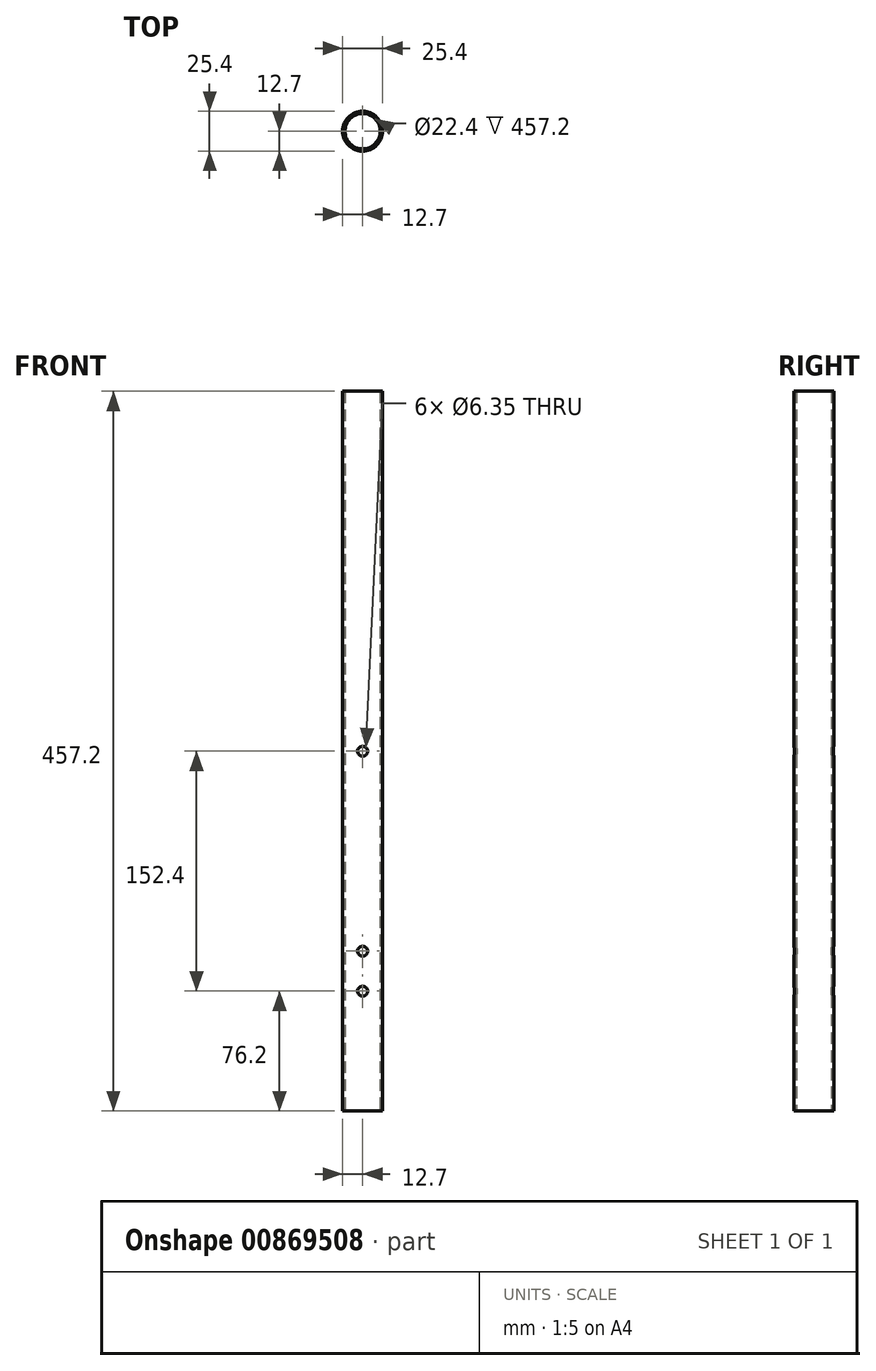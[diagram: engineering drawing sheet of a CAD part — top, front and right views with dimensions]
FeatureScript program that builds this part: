
annotation { "Feature Type Name" : "Feature", "Feature Type Description" : "" }
export const myFeature = defineFeature(function(context is Context, id is Id, definition is map)
    precondition{}
    {
        {
            var Q0;
            Q0=qCreatedBy(makeId("Top.planeOp"),FACE);
            var sketch = newSketch(context, id + "F0", { "sketchPlane" : qUnion([Q0])});
            skCircle(sketch, "E0", {"center": v(0, 0) * mm, "radius": 12.7 * mm});
            skCircle(sketch, "E1.0", {"center": v(0, 0) * mm, "radius": 11.2 * mm});
            skSolve(sketch);
        }
        {
            var Q0;
            Q0=makeQuery(id+"F0.imprint","IMPRINT",FACE,{"disambiguationData":[TD([[makeQuery(id+"F0.imprint","IMPRINT",EDGE,{"derivedFrom":sQuery(id+"F0.wireOp",EDGE,"E0")}),1.0]])]});
            extrude(context, id + "F1", {"entities" : qUnion([Q0]), "depth" : 457.2 * mm, "offsetDistance" : 25.4 * mm});
        }
        {
            var Q0;
            Q0=qCreatedBy(makeId("Front.planeOp"),FACE);
            var sketch = newSketch(context, id + "F2", { "sketchPlane" : qUnion([Q0])});
            skLineSegment(sketch, "E2", {"start": v(0, 0) * mm, "end": v(0, 457.2) * mm, "construction": true});
            skCircle(sketch, "E3", {"center": v(0, 76.2) * mm, "radius": 3.18 * mm});
            skCircle(sketch, "E4", {"center": v(0, 228.6) * mm, "radius": 3.18 * mm});
            skCircle(sketch, "E5", {"center": v(0, 101.6) * mm, "radius": 3.18 * mm});
            skSolve(sketch);
        }
        {
            var Q0;
            Q0 = qSketchRegion(id + "F2", true);
            extrude(context, id + "F3", {"entities" : qUnion([Q0]), "operationType" : NewBodyOperationType.REMOVE, "endBound" : BoundingType.SYMMETRIC, "depth" : 25.4 * mm, "offsetDistance" : 25.4 * mm});
        }
    });
